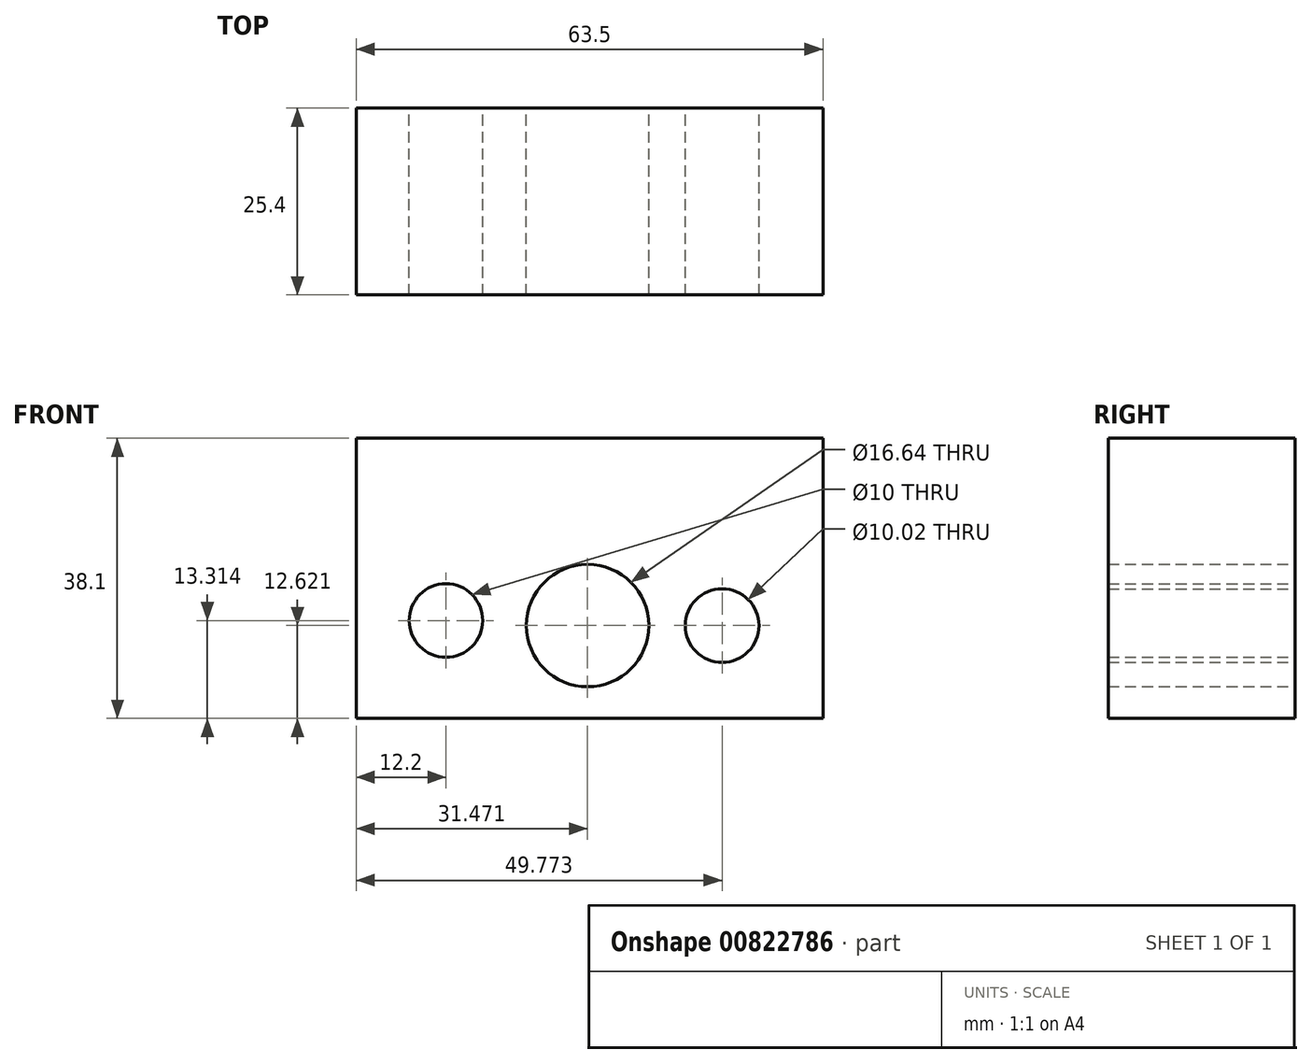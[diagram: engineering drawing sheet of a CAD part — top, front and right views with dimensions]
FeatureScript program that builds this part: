
annotation { "Feature Type Name" : "Feature", "Feature Type Description" : "" }
export const myFeature = defineFeature(function(context is Context, id is Id, definition is map)
    precondition{}
    {
        {
            var Q0;
            Q0=qCreatedBy(makeId("Front.planeOp"),FACE);
            var sketch = newSketch(context, id + "F0", { "sketchPlane" : qUnion([Q0])});
            skLineSegment(sketch, "E0", {"start": v(-38.61, 55.74) * mm, "end": v(-38.61, 17.64) * mm});
            skLineSegment(sketch, "E1", {"start": v(-38.61, 17.64) * mm, "end": v(24.89, 17.64) * mm});
            skLineSegment(sketch, "E2", {"start": v(24.89, 17.64) * mm, "end": v(24.89, 55.74) * mm});
            skLineSegment(sketch, "E3", {"start": v(-38.61, 55.74) * mm, "end": v(24.89, 55.74) * mm});
            skCircle(sketch, "E4", {"center": v(-7.14, 30.26) * mm, "radius": 8.32 * mm});
            skCircle(sketch, "E5", {"center": v(-26.41, 30.95) * mm, "radius": 5 * mm});
            skCircle(sketch, "E6", {"center": v(11.16, 30.26) * mm, "radius": 5 * mm});
            skSolve(sketch);
        }
        {
            var Q0;
            Q0 = qSketchRegion(id + "F0", true);
            extrude(context, id + "F1", {"entities" : qUnion([Q0]), "depth" : 25.4 * mm, "offsetDistance" : 25.4 * mm});
        }
    });
